# Revit family: FP_Revit_18_RF306RDWX1_Wine_Cabinets_90001125A
name_source: partatom
category: Specialty Equipment
revit_build: Autodesk Revit 2018 (Build: 20170223_1515(x64)
units: mm (PartAtom-declared; Revit-internal decimal feet)

## family parameters
Always vertical = Yes
Cut with Voids When Loaded = Yes
OmniClass Number = 23.40.40.11.11.17
OmniClass Title = Refrigerator-Freezer
Part Type = Normal
Room Calculation Point = No
Round Connector Dimension = Use Diameter
Shared = No
Work Plane-Based = No

## types (4) — shared parameters
Cavity - Depth = 669 mm  [stored 2.19488 ft]
Cavity - Width = 635 mm
Connector Description - Electrical = 230 V, 15 A, fused electrical supply
Manufacturer = Fisher & Paykel Appliances
Material - Body = Fisher & Paykel - Grey
Material - Door Front = Fisher & Paykel - Stainless Steel
Material - Door Glass = Fisher & Paykel - Black
Material - Handle = Fisher & Paykel - Aluminium
Material - Trim = Fisher & Paykel - Black
Product - Depth = 690 mm  [stored 2.26378 ft]
Product - Width = 595 mm  [stored 1.9521 ft]
URL = www.fisherpaykel.com
Visibility - Clearance Required = Yes

## per-type parameters (varying)
| type | Cavity - Height | Description | Model | Product - Height |
| RF106RDWX1 | 875 mm  [stored 2.87073 ft] | Wine Cabinet - 50 Bottle Dual Zone | RF106RDWX1 | 825 mm  [stored 2.70669 ft] |
| RF206RDWX1 | 1320 mm | Wine Cabinet - 83 Bottle Dual Zone | RF206RDWX1 | 1270 mm |
| RF306RDWX1 | 1710 mm  [stored 5.61024 ft] | Wine Cabinet - 127 Bottle Dual Zone | RF306RDWX1 | 1660 mm  [stored 5.44619 ft] |
| RF365RDWX1 | 1905 mm  [stored 6.25 ft] | Wine Cabinet - 144 Bottle Dual Zone | RF356RDWX1 | 1855 mm  [stored 6.08596 ft] |

note: [stored X ft] marks values corroborated as IEEE doubles in the binary element streams (Revit-internal decimal feet)

## geometry (parser evidence)
native form markers: Sweep x2
no freeform markers — native parametric forms only
